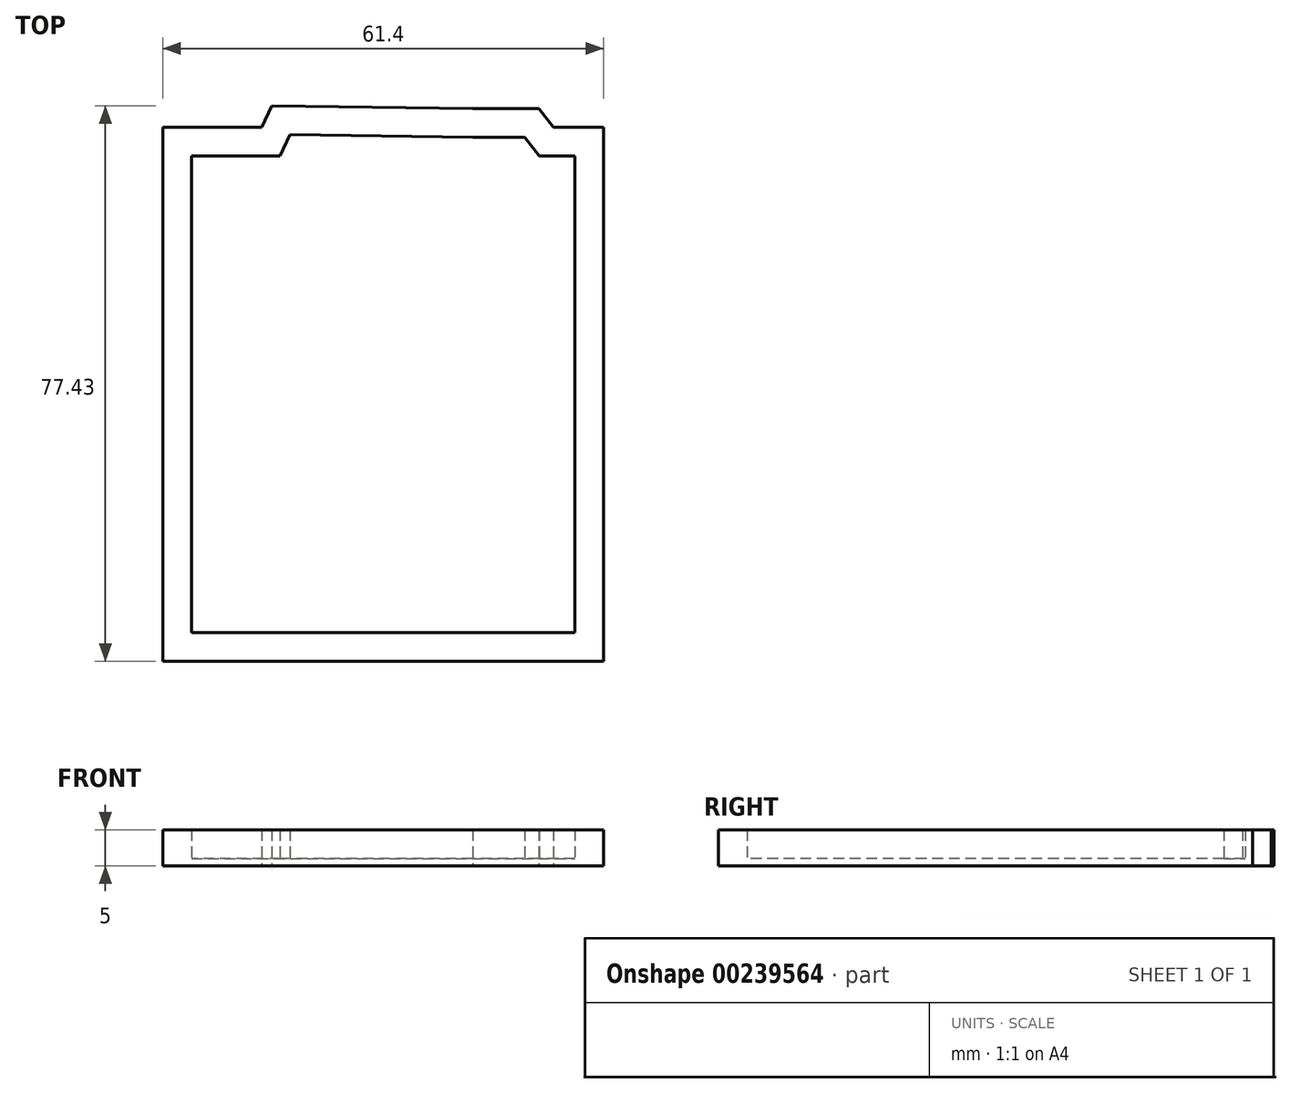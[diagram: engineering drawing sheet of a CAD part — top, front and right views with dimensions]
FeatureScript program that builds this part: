
annotation { "Feature Type Name" : "Feature", "Feature Type Description" : "" }
export const myFeature = defineFeature(function(context is Context, id is Id, definition is map)
    precondition{}
    {
        {
            var Q0;
            Q0=qCreatedBy(makeId("Top.planeOp"),FACE);
            var sketch = newSketch(context, id + "F0", { "sketchPlane" : qUnion([Q0])});
            skLineSegment(sketch, "E0", {"start": v(-31.2, 0) * mm, "end": v(22.2, 0) * mm});
            skLineSegment(sketch, "E1", {"start": v(22.2, 0) * mm, "end": v(22.2, 66.4) * mm});
            skLineSegment(sketch, "E2", {"start": v(22.2, 66.4) * mm, "end": v(17.23, 66.4) * mm});
            skLineSegment(sketch, "E3", {"start": v(17.23, 66.4) * mm, "end": v(15.21, 69.02) * mm});
            skLineSegment(sketch, "E4", {"start": v(15.21, 69.02) * mm, "end": v(7.94, 69.02) * mm});
            skLineSegment(sketch, "E5", {"start": v(7.94, 69.02) * mm, "end": v(-17.49, 69.4) * mm});
            skLineSegment(sketch, "E6", {"start": v(-17.49, 69.4) * mm, "end": v(-18.89, 66.4) * mm});
            skLineSegment(sketch, "E7", {"start": v(-18.89, 66.4) * mm, "end": v(-31.6, 66.4) * mm});
            skLineSegment(sketch, "E8", {"start": v(-31.2, 66.4) * mm, "end": v(-31.6, 66.4) * mm});
            skLineSegment(sketch, "E9", {"start": v(-31.2, 66.4) * mm, "end": v(-31.2, 0) * mm});
            skLineSegment(sketch, "E10.0", {"start": v(17.18, 73.02) * mm, "end": v(7.96, 73.02) * mm});
            skLineSegment(sketch, "E10.1", {"start": v(19.2, 70.4) * mm, "end": v(17.18, 73.02) * mm});
            skLineSegment(sketch, "E10.2", {"start": v(7.96, 73.02) * mm, "end": v(-20.01, 73.43) * mm});
            skLineSegment(sketch, "E10.3", {"start": v(26.2, 70.4) * mm, "end": v(19.2, 70.4) * mm});
            skLineSegment(sketch, "E10.4", {"start": v(26.2, -4) * mm, "end": v(26.2, 70.4) * mm});
            skLineSegment(sketch, "E10.5", {"start": v(-35.2, -4) * mm, "end": v(26.2, -4) * mm});
            skLineSegment(sketch, "E10.6", {"start": v(-20.01, 73.43) * mm, "end": v(-21.43, 70.4) * mm});
            skLineSegment(sketch, "E10.7", {"start": v(-21.43, 70.4) * mm, "end": v(-31.6, 70.4) * mm});
            skLineSegment(sketch, "E10.8", {"start": v(-31.6, 70.4) * mm, "end": v(-35.2, 70.4) * mm});
            skLineSegment(sketch, "E10.9", {"start": v(-35.2, 70.4) * mm, "end": v(-35.2, -4) * mm});
            skSolve(sketch);
        }
        {
            var Q0;
            Q0=makeQuery(id+"F0.imprint","IMPRINT",FACE,{"disambiguationData":[TD([[makeQuery(id+"F0.imprint","IMPRINT",EDGE,{"derivedFrom":sQuery(id+"F0.wireOp",EDGE,"E0")}),-1.0]])]});
            extrude(context, id + "F1", {"entities" : qUnion([Q0]), "depth" : 5 * mm});
        }
        {
            var Q0;
            Q0=makeQuery(id+"F0.imprint","IMPRINT",FACE,{"disambiguationData":[TD([[makeQuery(id+"F0.imprint","IMPRINT",EDGE,{"derivedFrom":sQuery(id+"F0.wireOp",EDGE,"E0")}),1.0]])]});
            extrude(context, id + "F2", {"entities" : qUnion([Q0]), "operationType" : NewBodyOperationType.ADD, "depth" : 1 * mm});
        }
    });
